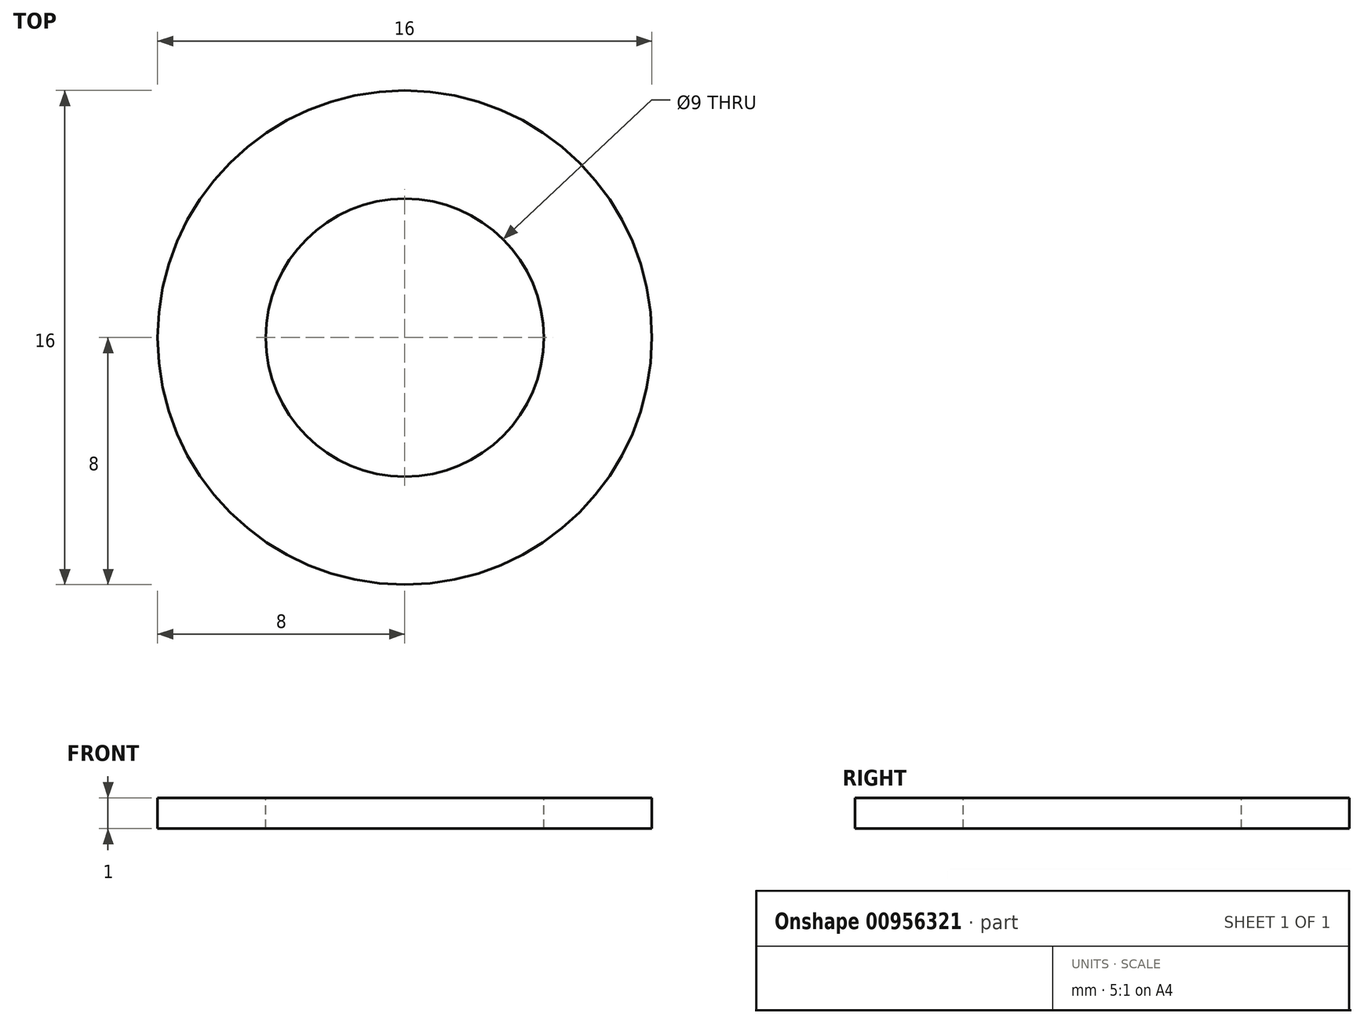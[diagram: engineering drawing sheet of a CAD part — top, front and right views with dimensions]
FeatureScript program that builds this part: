
annotation { "Feature Type Name" : "Feature", "Feature Type Description" : "" }
export const myFeature = defineFeature(function(context is Context, id is Id, definition is map)
    precondition{}
    {
        {
            var Q0;
            Q0=qCreatedBy(makeId("Top.planeOp"),FACE);
            var sketch = newSketch(context, id + "F0", { "sketchPlane" : qUnion([Q0])});
            skCircle(sketch, "E0", {"center": v(0, 0) * mm, "radius": 4.5 * mm});
            skCircle(sketch, "E1", {"center": v(0, 0) * mm, "radius": 8 * mm});
            skSolve(sketch);
        }
        {
            var Q0;
            Q0=qSketchRegion(id+"F0",true);
            extrude(context, id + "F1", {"entities" : qUnion([Q0]), "oppositeDirection" : true, "depth" : 1 * mm, "offsetDistance" : 25 * mm});
        }
    });
